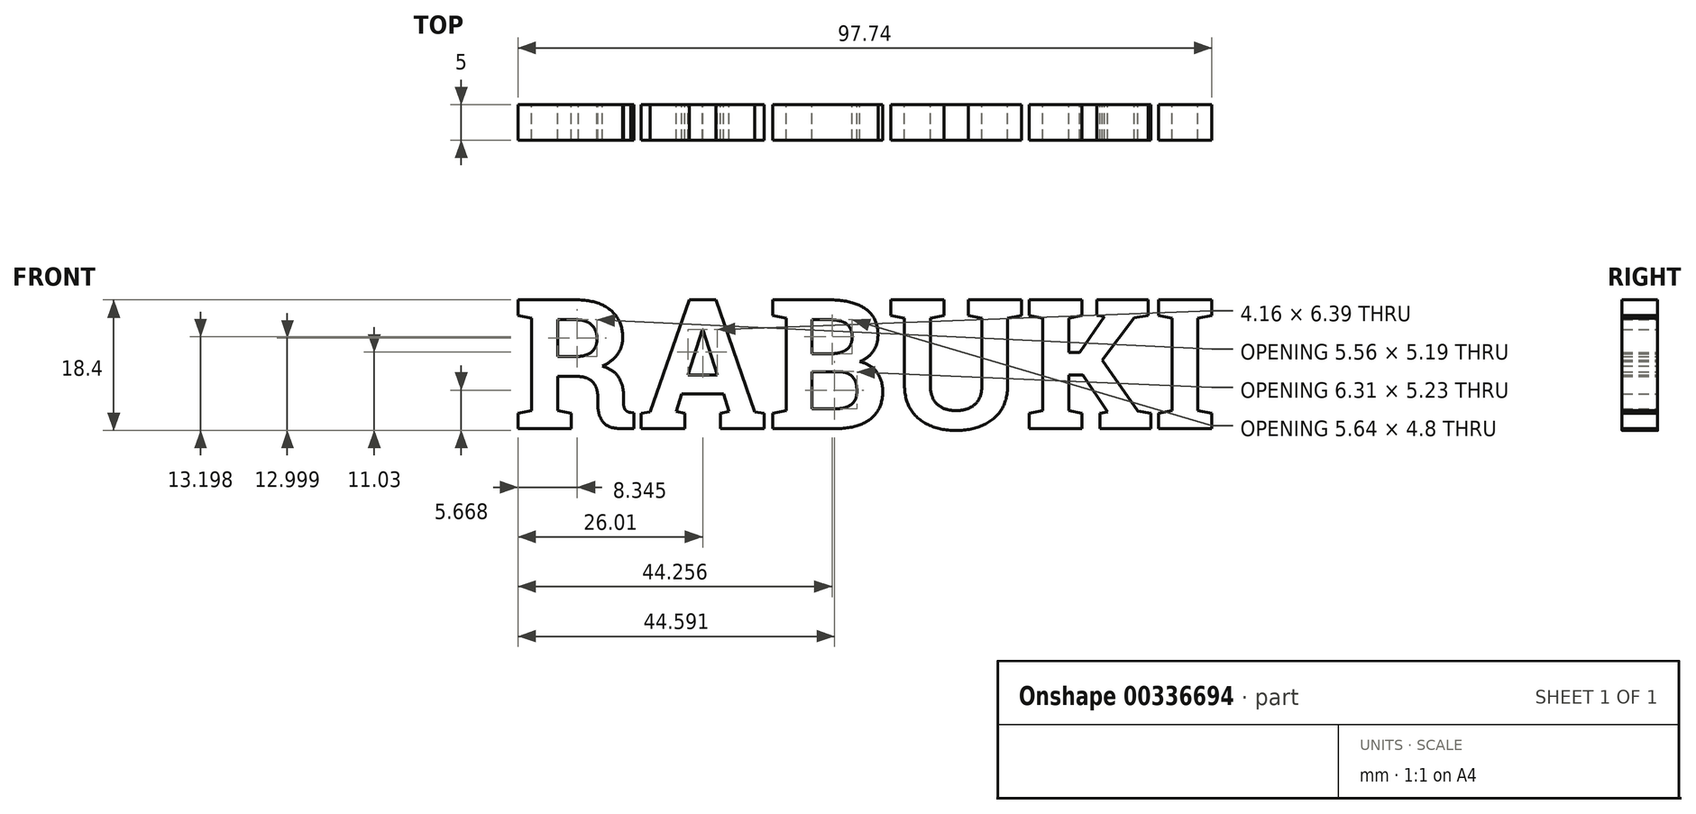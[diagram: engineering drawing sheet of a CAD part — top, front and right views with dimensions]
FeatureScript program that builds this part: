
annotation { "Feature Type Name" : "Feature", "Feature Type Description" : "" }
export const myFeature = defineFeature(function(context is Context, id is Id, definition is map)
    precondition{}
    {
        {
            var Q0;
            Q0=qCreatedBy(makeId("Front.planeOp"),FACE);
            var sketch = newSketch(context, id + "F0", { "sketchPlane" : qUnion([Q0])});
            skText(sketch, "E0", { "text": "RABUKI", "fontName": "RobotoSlab-Bold.ttf"});
            const initialGuessF0  = {"E0": [-0.04576, -0.0141, 1, 0, 0.01837]};
            skSetInitialGuess(sketch, initialGuessF0);
            skSolve(sketch);
        }
        {
            var Q0;
            Q0=makeQuery(id+"F0.imprint","IMPRINT",FACE,{"disambiguationData":[TD([[makeQuery(id+"F0.imprint","IMPRINT",EDGE,{"derivedFrom":sQuery(id+"F0.wireOp",EDGE,"E0.sketch_text.stroke-0")}),-1.0]])]});
            var Q1;
            Q1=makeQuery(id+"F0.imprint","IMPRINT",FACE,{"disambiguationData":[TD([[makeQuery(id+"F0.imprint","IMPRINT",EDGE,{"derivedFrom":sQuery(id+"F0.wireOp",EDGE,"E0.sketch_text.stroke-36")}),-1.0]])]});
            var Q2;
            Q2=makeQuery(id+"F0.imprint","IMPRINT",FACE,{"disambiguationData":[TD([[makeQuery(id+"F0.imprint","IMPRINT",EDGE,{"derivedFrom":sQuery(id+"F0.wireOp",EDGE,"E0.sketch_text.stroke-56")}),-1.0]])]});
            var Q3;
            Q3=makeQuery(id+"F0.imprint","IMPRINT",FACE,{"disambiguationData":[TD([[makeQuery(id+"F0.imprint","IMPRINT",EDGE,{"derivedFrom":sQuery(id+"F0.wireOp",EDGE,"E0.sketch_text.stroke-86")}),-1.0]])]});
            var Q4;
            Q4=makeQuery(id+"F0.imprint","IMPRINT",FACE,{"disambiguationData":[TD([[makeQuery(id+"F0.imprint","IMPRINT",EDGE,{"derivedFrom":sQuery(id+"F0.wireOp",EDGE,"E0.sketch_text.stroke-110")}),-1.0]])]});
            var Q5;
            Q5=makeQuery(id+"F0.imprint","IMPRINT",FACE,{"disambiguationData":[TD([[makeQuery(id+"F0.imprint","IMPRINT",EDGE,{"derivedFrom":sQuery(id+"F0.wireOp",EDGE,"E0.sketch_text.stroke-139")}),-1.0]])]});
            extrude(context, id + "F1", {"entities" : qUnion([Q0, Q1, Q2, Q3, Q4, Q5]), "depth" : 5 * mm});
        }
    });
